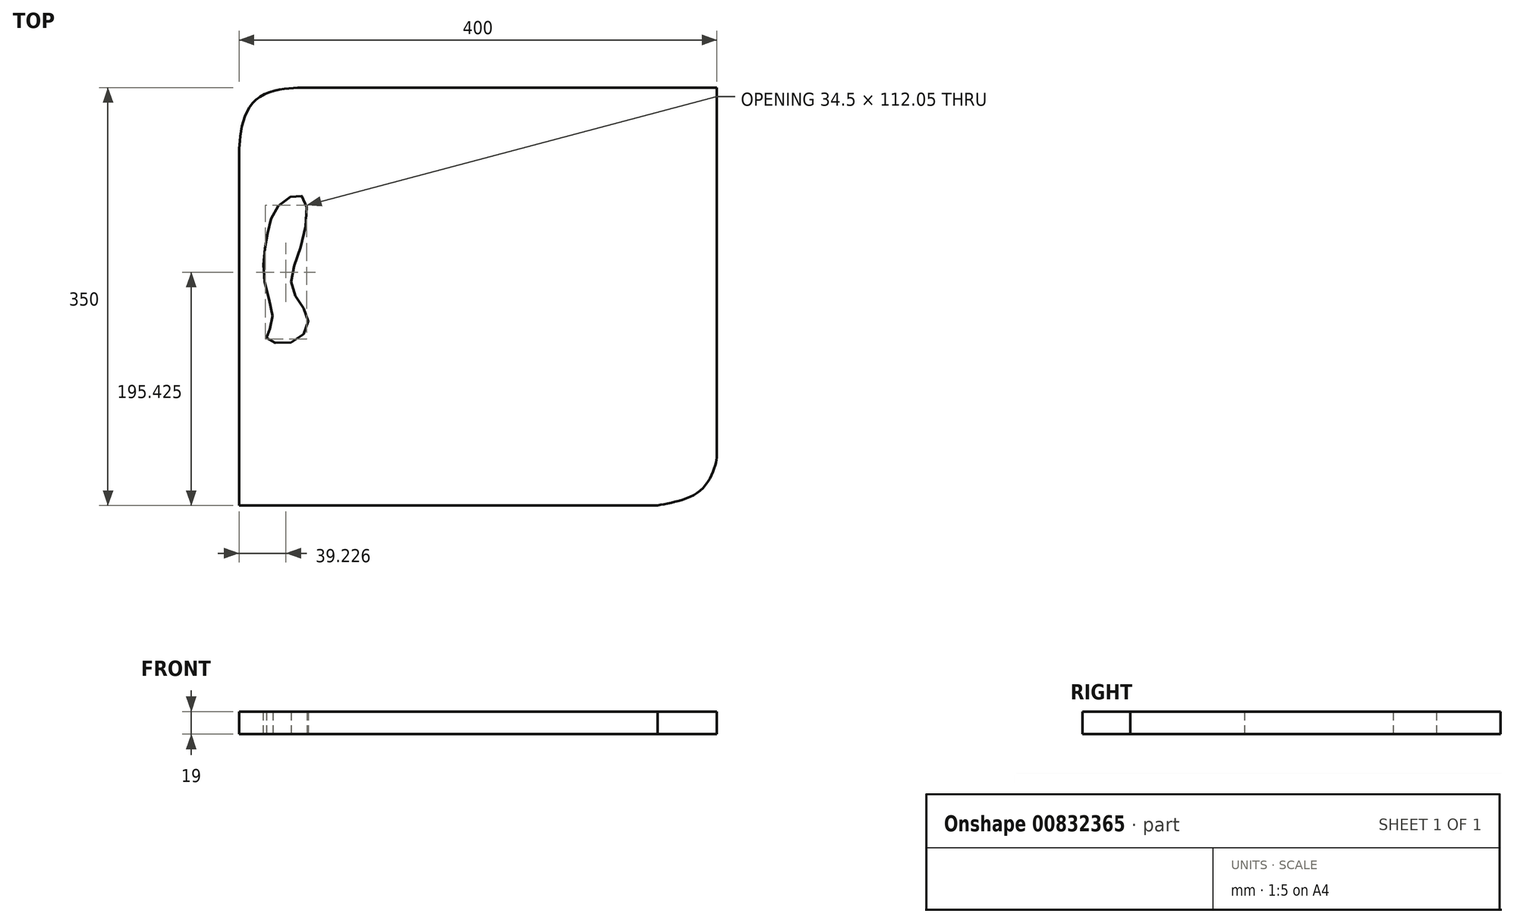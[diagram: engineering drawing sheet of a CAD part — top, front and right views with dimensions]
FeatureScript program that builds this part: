
annotation { "Feature Type Name" : "Feature", "Feature Type Description" : "" }
export const myFeature = defineFeature(function(context is Context, id is Id, definition is map)
    precondition{}
    {
        {
            var Q0;
            Q0=qCreatedBy(makeId("Top.planeOp"),FACE);
            var sketch = newSketch(context, id + "F0", { "sketchPlane" : qUnion([Q0])});
            skLineSegment(sketch, "E0.bottom", {"start": v(-200, 175) * mm, "end": v(200, 175) * mm});
            skLineSegment(sketch, "E0.top", {"start": v(-200, -175) * mm, "end": v(200, -175) * mm});
            skLineSegment(sketch, "E0.left", {"start": v(-200, 175) * mm, "end": v(-200, -175) * mm});
            skLineSegment(sketch, "E0.right", {"start": v(200, 175) * mm, "end": v(200, -175) * mm});
            skPoint(sketch, "E0.middle", {"position": v(0, 0) * mm});
            skSolve(sketch);
        }
        {
            var Q0;
            Q0=makeQuery(id+"F0.imprint","IMPRINT",FACE,{"disambiguationData":[TD([[makeQuery(id+"F0.imprint","IMPRINT",EDGE,{"derivedFrom":sQuery(id+"F0.wireOp",EDGE,"E0.bottom")}),-1.0]])]});
            extrude(context, id + "F1", {"entities" : qUnion([Q0]), "depth" : 19 * mm, "offsetDistance" : 25 * mm});
        }
        {
            var Q0;
            Q0=makeQuery(id+"F1.opExtrude","CAP_FACE",FACE,{"disambiguationData":[OSD([sQuery(id+"F0.wireOp",EDGE,"E0.bottom"),sQuery(id+"F0.wireOp",EDGE,"E0.top"),sQuery(id+"F0.wireOp",EDGE,"E0.left"),sQuery(id+"F0.wireOp",EDGE,"E0.right")])],"isStart":false});
            var sketch = newSketch(context, id + "F2", { "sketchPlane" : qUnion([Q0])});
            skFitSpline(sketch, "E1", {"points": [v(-145.7, 175) * mm, v(-187.12, 163.71) * mm, v(-200, 121.62) * mm, v(-200, 115.12) * mm], "startDerivative": vector(-57.67, 0) * mm, "endDerivative": vector(5.87, -36.7) * mm});
            skSolve(sketch);
        }
        {
            var Q0;
            {var subQ0=sQuery(id+"F2.wireOp",EDGE,"E1");var subQ1=makeQuery(id+"F1.opExtrude","CAP_EDGE",EDGE,{"disambiguationData":[OSD([sQuery(id+"F0.wireOp",EDGE,"E0.bottom")])],"isStart":false});var subQ2=makeQuery(id+"F2.imprint","INTERSECT",VERTEX,{"derivedFrom":[subQ1,subQ0]});Q0=makeQuery(id+"F2.imprint","IMPRINT",FACE,{"disambiguationData":[TD([[makeQuery(id+"F2.imprint","IMPRINT",EDGE,{"disambiguationData":[TD([[subQ2,-1.0]])],"derivedFrom":subQ0}),-1.0]])]});}
            extrude(context, id + "F3", {"entities" : qUnion([Q0]), "operationType" : NewBodyOperationType.REMOVE, "endBound" : BoundingType.THROUGH_ALL, "oppositeDirection" : true, "depth" : 25 * mm, "offsetDistance" : 25 * mm});
        }
        {
            var Q0;
            Q0=makeQuery(id+"F1.opExtrude","CAP_FACE",FACE,{"disambiguationData":[OSD([sQuery(id+"F0.wireOp",EDGE,"E0.bottom"),sQuery(id+"F0.wireOp",EDGE,"E0.top"),sQuery(id+"F0.wireOp",EDGE,"E0.left"),sQuery(id+"F0.wireOp",EDGE,"E0.right")])],"isStart":false});
            var sketch = newSketch(context, id + "F4", { "sketchPlane" : qUnion([Q0])});
            skFitSpline(sketch, "E2", {"points": [v(150.18, -175) * mm, v(186.44, -162.14) * mm, v(200, -134.94) * mm, v(200, -131.06) * mm], "startDerivative": vector(68.25, 15.53) * mm, "endDerivative": vector(-4.15, 12.44) * mm});
            skSolve(sketch);
        }
        {
            var Q0;
            {var subQ0=sQuery(id+"F4.wireOp",EDGE,"E2");var subQ1=makeQuery(id+"F1.opExtrude","CAP_EDGE",EDGE,{"disambiguationData":[OSD([sQuery(id+"F0.wireOp",EDGE,"E0.top")])],"isStart":false});var subQ2=makeQuery(id+"F4.imprint","INTERSECT",VERTEX,{"derivedFrom":[subQ1,subQ0]});Q0=makeQuery(id+"F4.imprint","IMPRINT",FACE,{"disambiguationData":[TD([[makeQuery(id+"F4.imprint","IMPRINT",EDGE,{"disambiguationData":[TD([[subQ2,-1.0]])],"derivedFrom":subQ0}),-1.0]])]});}
            extrude(context, id + "F5", {"entities" : qUnion([Q0]), "operationType" : NewBodyOperationType.REMOVE, "endBound" : BoundingType.THROUGH_ALL, "oppositeDirection" : true, "depth" : 25 * mm, "offsetDistance" : 25 * mm});
        }
        {
            var Q0;
            Q0=makeQuery(id+"F1.opExtrude","CAP_FACE",FACE,{"disambiguationData":[OSD([sQuery(id+"F0.wireOp",EDGE,"E0.bottom"),sQuery(id+"F0.wireOp",EDGE,"E0.top"),sQuery(id+"F0.wireOp",EDGE,"E0.left"),sQuery(id+"F0.wireOp",EDGE,"E0.right")])],"isStart":false});
            var sketch = newSketch(context, id + "F6", { "sketchPlane" : qUnion([Q0])});
            skFitSpline(sketch, "E3", {"points": [v(-167.12, 75.81) * mm, v(-176.7, 49.32) * mm, v(-178.96, 14.37) * mm, v(-172.2, -22.26) * mm, v(-176.7, -35.23) * mm, v(-154.16, -37.48) * mm, v(-142.32, -17.75) * mm, v(-155.85, 7.05) * mm, v(-146.83, 47.06) * mm, v(-147.4, 84.27) * mm, v(-167.12, 75.81) * mm]});
            skSolve(sketch);
        }
        {
            var Q0;
            Q0=makeQuery(id+"F6.imprint","IMPRINT",FACE,{"disambiguationData":[TD([[makeQuery(id+"F6.imprint","IMPRINT",EDGE,{"derivedFrom":sQuery(id+"F6.wireOp",EDGE,"E3")}),1.0]])]});
            extrude(context, id + "F7", {"entities" : qUnion([Q0]), "operationType" : NewBodyOperationType.REMOVE, "endBound" : BoundingType.THROUGH_ALL, "oppositeDirection" : true, "depth" : 25 * mm, "offsetDistance" : 25 * mm});
        }
    });
